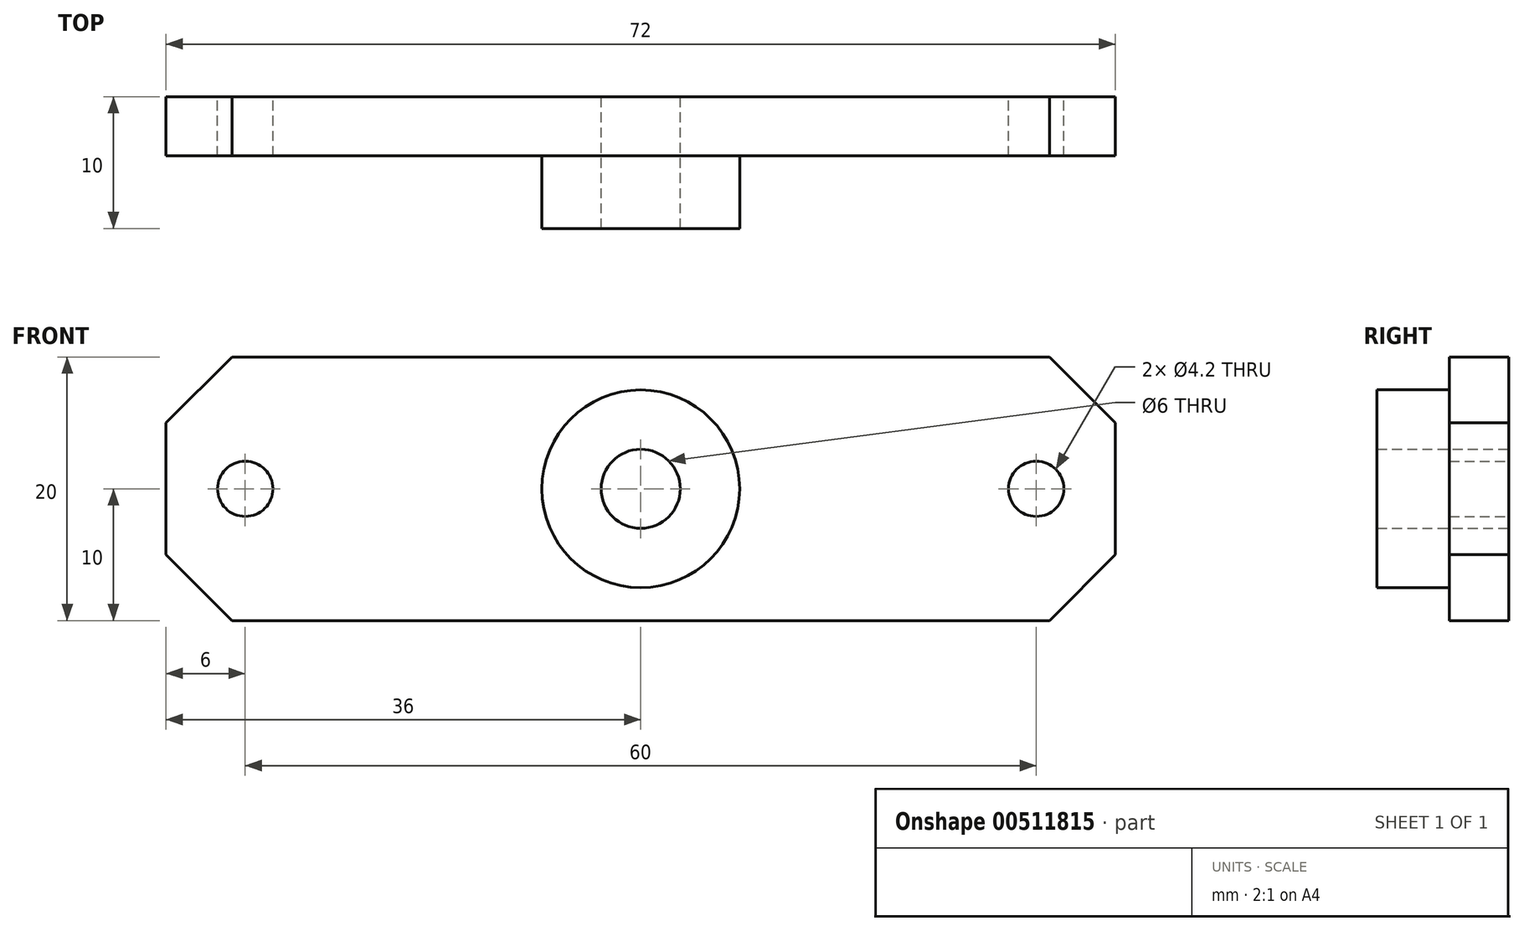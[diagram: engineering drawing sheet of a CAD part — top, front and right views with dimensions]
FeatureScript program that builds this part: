
annotation { "Feature Type Name" : "Feature", "Feature Type Description" : "" }
export const myFeature = defineFeature(function(context is Context, id is Id, definition is map)
    precondition{}
    {
        {
            var Q0;
            Q0=qCreatedBy(makeId("Front.planeOp"),FACE);
            var sketch = newSketch(context, id + "F0", { "sketchPlane" : qUnion([Q0])});
            skLineSegment(sketch, "E0.bottom", {"start": v(36, 10) * mm, "end": v(-36, 10) * mm});
            skLineSegment(sketch, "E0.top", {"start": v(36, -10) * mm, "end": v(-36, -10) * mm});
            skLineSegment(sketch, "E0.left", {"start": v(36, 10) * mm, "end": v(36, -10) * mm});
            skLineSegment(sketch, "E0.right", {"start": v(-36, 10) * mm, "end": v(-36, -10) * mm});
            skPoint(sketch, "E0.middle", {"position": v(0, 0) * mm});
            skCircle(sketch, "E1", {"center": v(0, 0) * mm, "radius": 3 * mm});
            skLineSegment(sketch, "E2", {"start": v(0, 32.36) * mm, "end": v(0, -28.18) * mm, "construction": true});
            skPoint(sketch, "E3.MirrorP", {"position": v(-30, -0.01) * mm});
            skPoint(sketch, "E4.MirrorP", {"position": v(30, -0.01) * mm});
            skSolve(sketch);
        }
        {
            var Q0;
            Q0=qSketchRegion(id+"F0",true);
            extrude(context, id + "F1", {"entities" : qUnion([Q0]), "depth" : 4.5 * mm});
        }
        {
            var Q0;
            Q0=makeQuery(id+"F1.opExtrude","CAP_FACE",FACE,{"disambiguationData":[OSD([sQuery(id+"F0.wireOp",EDGE,"E0.bottom"),sQuery(id+"F0.wireOp",EDGE,"E0.top"),sQuery(id+"F0.wireOp",EDGE,"E0.left"),sQuery(id+"F0.wireOp",EDGE,"E0.right"),sQuery(id+"F0.wireOp",EDGE,"E1"),sQuery(id+"F0.wireOp",EDGE,"ENy42JfF-6w3e-OXzw-JDkE-4kl2GYuJj7oi"),sQuery(id+"F0.wireOp",EDGE,"80a0704a-bb5c-43a5-97d3-b2e101dcfcec0.MirrorC")])],"isStart":false});
            var sketch = newSketch(context, id + "F2", { "sketchPlane" : qUnion([Q0])});
            skCircle(sketch, "E5", {"center": v(0, 0) * mm, "radius": 7.5 * mm});
            skSolve(sketch);
        }
        {
            var Q0;
            Q0=makeQuery(id+"F2.imprint","IMPRINT",FACE,{"disambiguationData":[TD([[makeQuery(id+"F2.imprint","IMPRINT",EDGE,{"derivedFrom":sQuery(id+"F2.wireOp",EDGE,"E5")}),1.0]])]});
            extrude(context, id + "F3", {"entities" : qUnion([Q0]), "operationType" : NewBodyOperationType.ADD, "depth" : 5.5 * mm});
        }
        {
            var Q0;
            Q0=makeQuery(id+"F1.opExtrude","SWEPT_EDGE",EDGE,{"disambiguationData":[OSD([sQuery(id+"F0.wireOp",EDGE,"E0.bottom"),sQuery(id+"F0.wireOp",EDGE,"E0.left")])]});
            var Q1;
            Q1=makeQuery(id+"F1.opExtrude","SWEPT_EDGE",EDGE,{"disambiguationData":[OSD([sQuery(id+"F0.wireOp",EDGE,"E0.top"),sQuery(id+"F0.wireOp",EDGE,"E0.left")])]});
            var Q2;
            Q2=makeQuery(id+"F1.opExtrude","SWEPT_EDGE",EDGE,{"disambiguationData":[OSD([sQuery(id+"F0.wireOp",EDGE,"E0.bottom"),sQuery(id+"F0.wireOp",EDGE,"E0.right")])]});
            var Q3;
            Q3=makeQuery(id+"F1.opExtrude","SWEPT_EDGE",EDGE,{"disambiguationData":[OSD([sQuery(id+"F0.wireOp",EDGE,"E0.top"),sQuery(id+"F0.wireOp",EDGE,"E0.right")])]});
            chamfer(context, id + "F4", {"entities" : qUnion([Q0, Q1, Q2, Q3]), "width" : 5 * mm, "tangentPropagation" : true});
        }
        {
            var Q0;
            Q0=makeQuery(id+"F1.opExtrude","CAP_FACE",FACE,{"disambiguationData":[OSD([sQuery(id+"F0.wireOp",EDGE,"E0.bottom"),sQuery(id+"F0.wireOp",EDGE,"E0.top"),sQuery(id+"F0.wireOp",EDGE,"E0.left"),sQuery(id+"F0.wireOp",EDGE,"E0.right"),sQuery(id+"F0.wireOp",EDGE,"E1")])],"isStart":true});
            var sketch = newSketch(context, id + "F5", { "sketchPlane" : qUnion([Q0])});
            skCircle(sketch, "E6", {"center": v(-30, 0) * mm, "radius": 2.09 * mm});
            skCircle(sketch, "E7.MirrorC", {"center": v(30, 0) * mm, "radius": 2.09 * mm});
            skSolve(sketch);
        }
        {
            var Q0;
            Q0=sQuery(id+"F5.wireOp",VERTEX,"E6.center");
            var Q1;
            Q1=sQuery(id+"F5.wireOp",VERTEX,"E7.MirrorC.center");
            var Q2;
            Q2=makeQuery(id+"F1.opExtrude","SWEPT_BODY",BODY,{"disambiguationData":[OSD([sQuery(id+"F0.wireOp",EDGE,"E0.bottom"),sQuery(id+"F0.wireOp",EDGE,"E0.top"),sQuery(id+"F0.wireOp",EDGE,"E0.left"),sQuery(id+"F0.wireOp",EDGE,"E0.right"),sQuery(id+"F0.wireOp",EDGE,"E1")])]});
            hole(context, id + "F6", {"style" : HoleStyle.SIMPLE, "endStyle" : HoleEndStyle.THROUGH, "standardTappedOrClearance" : lookupTablePath({ "standard" : "ISO", "engagement" : "75%", "pitch" : "0.8 mm", "size" : "M5", "type" : "Tapped" }), "standardBlindInLast" : lookupTablePath({ "standard" : "ISO", "engagement" : "75%", "pitch" : "0.8 mm", "size" : "M5", "type" : "Tapped" }), "holeDiameter" : 4.2 * mm, "showTappedDepth" : true, "isTappedThrough" : true, "tappedDepth" : 12 * mm, "tapClearance" : 3, "startFromSketch" : true, "locations" : qUnion([Q0, Q1]), "scope" : qUnion([Q2]), "majorDiameter" : 5 * mm});
        }
    });
